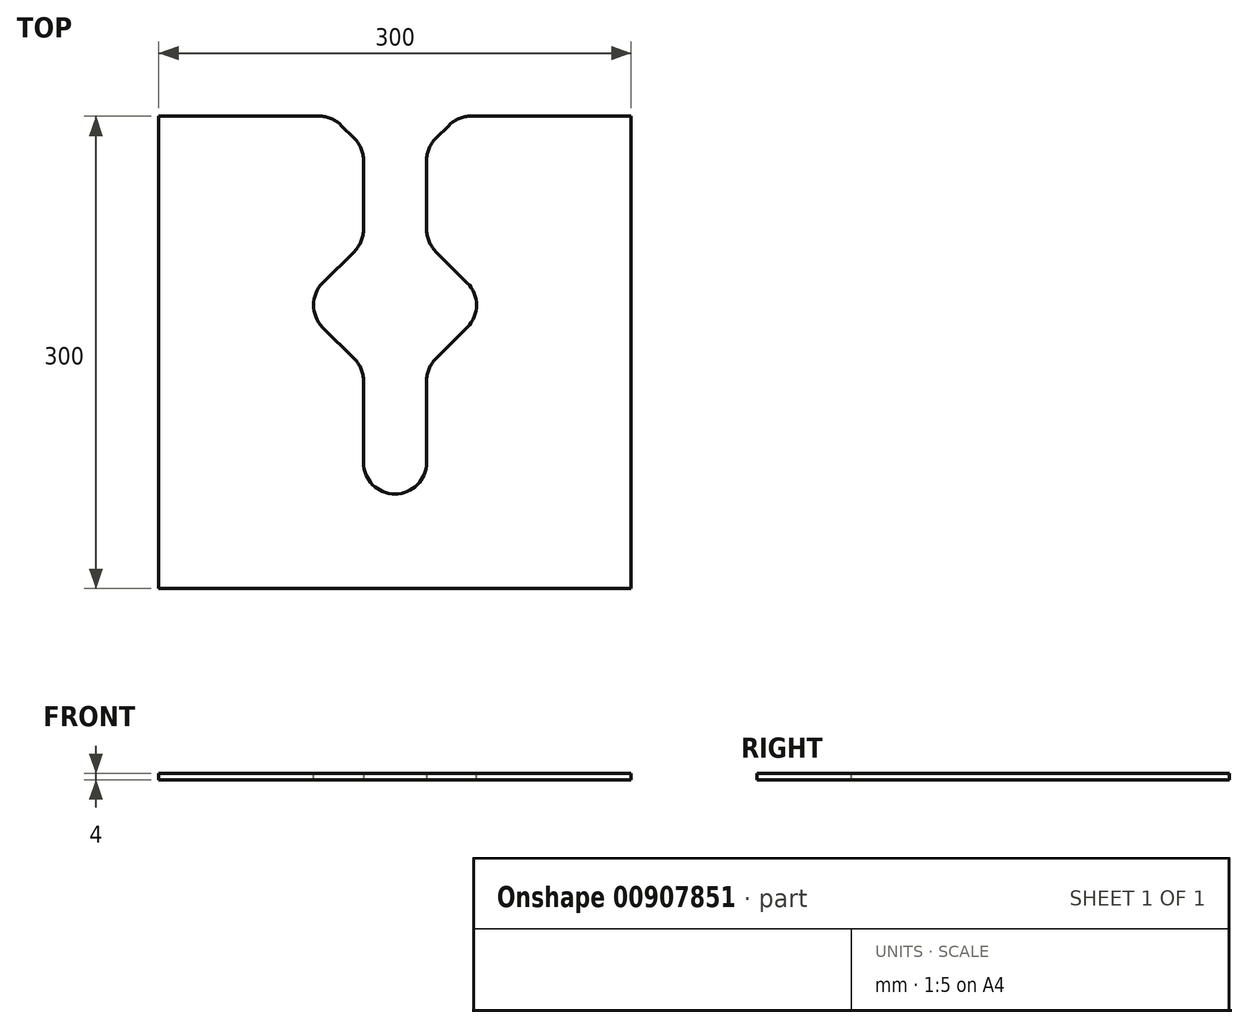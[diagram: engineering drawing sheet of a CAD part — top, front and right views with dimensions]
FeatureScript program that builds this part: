
annotation { "Feature Type Name" : "Feature", "Feature Type Description" : "" }
export const myFeature = defineFeature(function(context is Context, id is Id, definition is map)
    precondition{}
    {
        {
            var Q0;
            Q0=qCreatedBy(makeId("Top.planeOp"),FACE);
            var sketch = newSketch(context, id + "F0", { "sketchPlane" : qUnion([Q0])});
            skLineSegment(sketch, "E0.bottom", {"start": v(0, 0) * mm, "end": v(300, 0) * mm});
            skLineSegment(sketch, "E0.top", {"start": v(0, 300) * mm, "end": v(300, 300) * mm});
            skLineSegment(sketch, "E0.left", {"start": v(0, 0) * mm, "end": v(0, 300) * mm});
            skLineSegment(sketch, "E0.right", {"start": v(300, 0) * mm, "end": v(300, 300) * mm});
            skLineSegment(sketch, "E1", {"start": v(150, 60) * mm, "end": v(170, 60) * mm});
            skLineSegment(sketch, "E2", {"start": v(150, 60) * mm, "end": v(130, 60) * mm});
            skLineSegment(sketch, "E3", {"start": v(130, 60) * mm, "end": v(130, 300) * mm});
            skLineSegment(sketch, "E4", {"start": v(170, 60) * mm, "end": v(170, 300) * mm});
            skLineSegment(sketch, "E5", {"start": v(150, 0) * mm, "end": v(150, 300) * mm});
            skLineSegment(sketch, "E6", {"start": v(150, 0) * mm, "end": v(150, 180) * mm});
            skLineSegment(sketch, "E7", {"start": v(150, 180) * mm, "end": v(210, 180) * mm});
            skLineSegment(sketch, "E8", {"start": v(150, 180) * mm, "end": v(90, 180) * mm});
            skLineSegment(sketch, "E9", {"start": v(150, 180) * mm, "end": v(150, 120) * mm});
            skLineSegment(sketch, "E10", {"start": v(150, 180) * mm, "end": v(150, 240) * mm});
            skLineSegment(sketch, "E11", {"start": v(150, 240) * mm, "end": v(90, 180) * mm});
            skLineSegment(sketch, "E12", {"start": v(90, 180) * mm, "end": v(150, 120) * mm});
            skLineSegment(sketch, "E13", {"start": v(150, 120) * mm, "end": v(210, 180) * mm});
            skLineSegment(sketch, "E14", {"start": v(210, 180) * mm, "end": v(150, 240) * mm});
            skLineSegment(sketch, "E15", {"start": v(150, 300) * mm, "end": v(150, 260) * mm});
            skLineSegment(sketch, "E16", {"start": v(150, 300) * mm, "end": v(190, 300) * mm});
            skLineSegment(sketch, "E17", {"start": v(190, 300) * mm, "end": v(150, 260) * mm});
            skLineSegment(sketch, "E18", {"start": v(150, 300) * mm, "end": v(110, 300) * mm});
            skLineSegment(sketch, "E19", {"start": v(110, 300) * mm, "end": v(150, 260) * mm});
            skSolve(sketch);
        }
        {
            var Q0;
            {var subQ0=sQuery(id+"F0.wireOp",EDGE,"E0.left");Q0=makeQuery(id+"F0.imprint","IMPRINT",FACE,{"disambiguationData":[TD([[makeQuery(id+"F0.imprint","IMPRINT",EDGE,{"derivedFrom":subQ0}),-1.0]])]});}
            var Q1;
            {var subQ0=sQuery(id+"F0.wireOp",EDGE,"E0.right");Q1=makeQuery(id+"F0.imprint","IMPRINT",FACE,{"disambiguationData":[TD([[makeQuery(id+"F0.imprint","IMPRINT",EDGE,{"derivedFrom":subQ0}),1.0]])]});}
            extrude(context, id + "F1", {"entities" : qUnion([Q0, Q1]), "depth" : 4 * mm, "offsetDistance" : 25 * mm});
        }
        {
            var Q0;
            Q0=makeQuery(id+"F1.opExtrude","SWEPT_EDGE",EDGE,{"disambiguationData":[OSD([sQuery(id+"F0.wireOp",EDGE,"E2"),sQuery(id+"F0.wireOp",EDGE,"E3")])]});
            var Q1;
            Q1=makeQuery(id+"F1.opExtrude","SWEPT_EDGE",EDGE,{"disambiguationData":[OSD([sQuery(id+"F0.wireOp",EDGE,"E3"),sQuery(id+"F0.wireOp",EDGE,"E12")])]});
            var Q2;
            Q2=makeQuery(id+"F1.opExtrude","SWEPT_EDGE",EDGE,{"disambiguationData":[OSD([sQuery(id+"F0.wireOp",EDGE,"E8"),sQuery(id+"F0.wireOp",EDGE,"E11"),sQuery(id+"F0.wireOp",EDGE,"E12")])]});
            var Q3;
            Q3=makeQuery(id+"F1.opExtrude","SWEPT_EDGE",EDGE,{"disambiguationData":[OSD([sQuery(id+"F0.wireOp",EDGE,"E3"),sQuery(id+"F0.wireOp",EDGE,"E11")])]});
            var Q4;
            Q4=makeQuery(id+"F1.opExtrude","SWEPT_EDGE",EDGE,{"disambiguationData":[OSD([sQuery(id+"F0.wireOp",EDGE,"E3"),sQuery(id+"F0.wireOp",EDGE,"E19")])]});
            var Q5;
            Q5=makeQuery(id+"F1.opExtrude","SWEPT_EDGE",EDGE,{"disambiguationData":[OSD([sQuery(id+"F0.wireOp",EDGE,"E0.top"),sQuery(id+"F0.wireOp",EDGE,"E19")])]});
            fillet(context, id + "F2", {"entities" : qUnion([Q0, Q1, Q2, Q3, Q4, Q5]), "radius" : 20 * mm, "tangentPropagation" : true, "allowEdgeOverflow" : false});
        }
        {
            var Q0;
            Q0=makeQuery(id+"F1.opExtrude","SWEPT_EDGE",EDGE,{"disambiguationData":[OSD([sQuery(id+"F0.wireOp",EDGE,"E0.top"),sQuery(id+"F0.wireOp",EDGE,"E17")])]});
            var Q1;
            Q1=makeQuery(id+"F1.opExtrude","SWEPT_EDGE",EDGE,{"disambiguationData":[OSD([sQuery(id+"F0.wireOp",EDGE,"E4"),sQuery(id+"F0.wireOp",EDGE,"E17")])]});
            var Q2;
            Q2=makeQuery(id+"F1.opExtrude","SWEPT_EDGE",EDGE,{"disambiguationData":[OSD([sQuery(id+"F0.wireOp",EDGE,"E4"),sQuery(id+"F0.wireOp",EDGE,"E14")])]});
            var Q3;
            Q3=makeQuery(id+"F1.opExtrude","SWEPT_EDGE",EDGE,{"disambiguationData":[OSD([sQuery(id+"F0.wireOp",EDGE,"E7"),sQuery(id+"F0.wireOp",EDGE,"E13"),sQuery(id+"F0.wireOp",EDGE,"E14")])]});
            var Q4;
            Q4=makeQuery(id+"F1.opExtrude","SWEPT_EDGE",EDGE,{"disambiguationData":[OSD([sQuery(id+"F0.wireOp",EDGE,"E4"),sQuery(id+"F0.wireOp",EDGE,"E13")])]});
            var Q5;
            Q5=makeQuery(id+"F1.opExtrude","SWEPT_EDGE",EDGE,{"disambiguationData":[OSD([sQuery(id+"F0.wireOp",EDGE,"E1"),sQuery(id+"F0.wireOp",EDGE,"E4")])]});
            fillet(context, id + "F3", {"entities" : qUnion([Q0, Q1, Q2, Q3, Q4, Q5]), "radius" : 20 * mm, "tangentPropagation" : true, "allowEdgeOverflow" : false});
        }
    });
